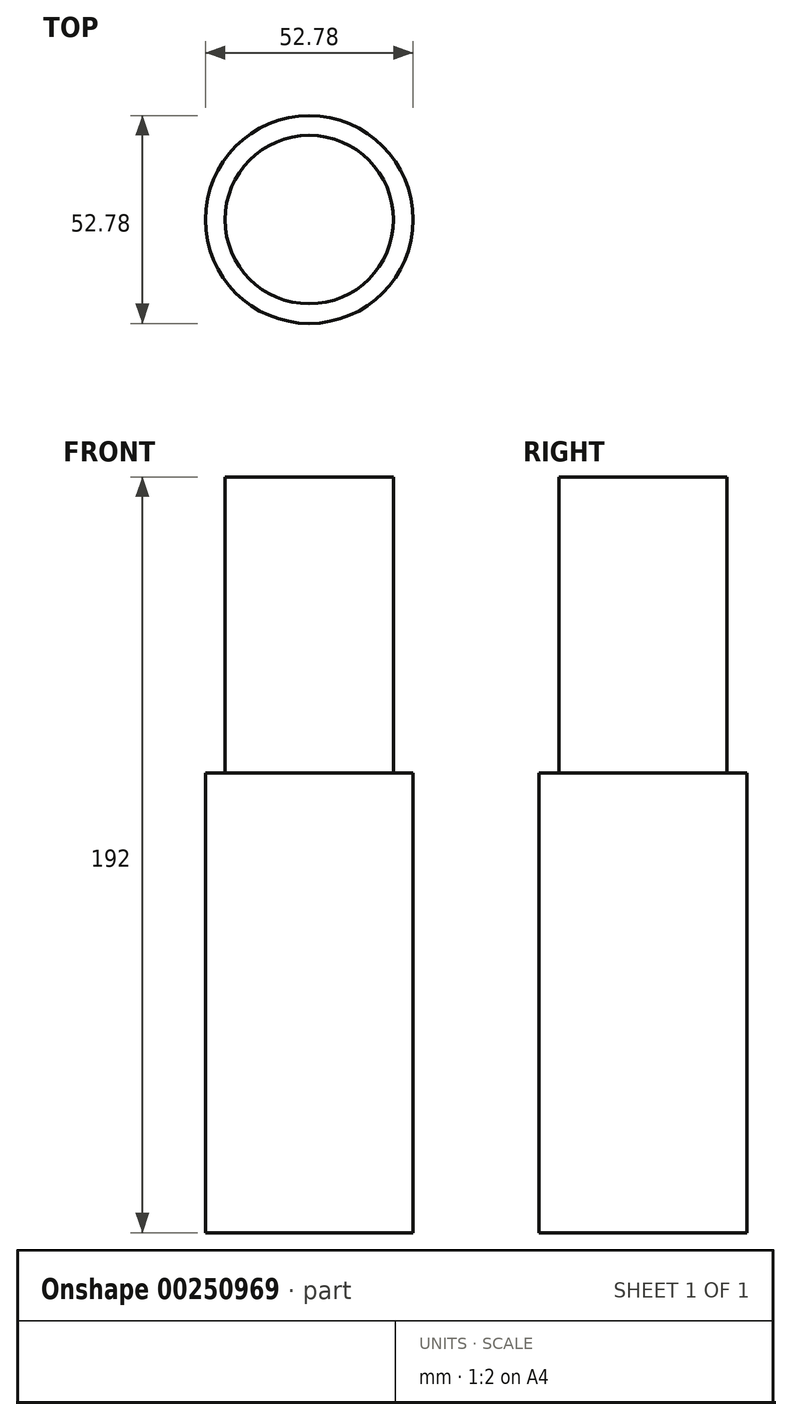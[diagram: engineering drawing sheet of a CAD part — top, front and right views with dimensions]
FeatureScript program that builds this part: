
annotation { "Feature Type Name" : "Feature", "Feature Type Description" : "" }
export const myFeature = defineFeature(function(context is Context, id is Id, definition is map)
    precondition{}
    {
        {
            var Q0;
            Q0=qCreatedBy(makeId("Front.planeOp"),FACE);
            var sketch = newSketch(context, id + "F0", { "sketchPlane" : qUnion([Q0])});
            skLineSegment(sketch, "E0.bottom", {"start": v(26.4, 58.38) * mm, "end": v(-26.4, 58.38) * mm});
            skLineSegment(sketch, "E0.top", {"start": v(26.4, -58.38) * mm, "end": v(-26.4, -58.38) * mm});
            skLineSegment(sketch, "E0.left", {"start": v(26.4, 58.38) * mm, "end": v(26.4, -58.38) * mm});
            skLineSegment(sketch, "E0.right", {"start": v(-26.4, 58.38) * mm, "end": v(-26.4, -58.38) * mm});
            skPoint(sketch, "E0.middle", {"position": v(0, 0) * mm});
            skLineSegment(sketch, "E1", {"start": v(0, 60.68) * mm, "end": v(0, -62.97) * mm});
            skPoint(sketch, "E1.startSnap0", {"position": v(0, 58.38) * mm});
            skSolve(sketch);
        }
        {
            var Q0;
            {var subQ0=sQuery(id+"F0.wireOp",EDGE,"E0.right");Q0=makeQuery(id+"F0.imprint","IMPRINT",FACE,{"disambiguationData":[TD([[makeQuery(id+"F0.imprint","IMPRINT",EDGE,{"derivedFrom":subQ0}),1.0]])]});}
            var Q1;
            Q1=sQuery(id+"F0.wireOp",EDGE,"E1");
            revolve(context, id + "F1", {"entities" : qUnion([Q0]), "axis" : qUnion([Q1]), "revolveType" : RevolveType.FULL});
        }
        {
            var Q0;
            Q0=makeQuery(id+"F1.opRevolve","SWEPT_FACE",FACE,{"disambiguationData":[OSD([sQuery(id+"F0.wireOp",EDGE,"E0.bottom")])]});
            shell(context, id + "F2", {"entities" : qUnion([Q0]), "thickness" : 5 * mm});
        }
        {
            var Q0;
            Q0=makeQuery(id+"F2.opShell","OFFSET_FACE",FACE,{"disambiguationData":[OSD([sQuery(id+"F0.wireOp",EDGE,"E0.top")])]});
            extrude(context, id + "F3", {"entities" : qUnion([Q0]), "operationType" : NewBodyOperationType.ADD, "depth" : 187 * mm});
        }
    });
